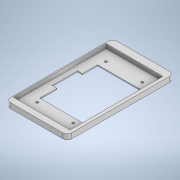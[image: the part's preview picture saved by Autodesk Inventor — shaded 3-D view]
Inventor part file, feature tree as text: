
AUTODESK INVENTOR PART (.ipt)
format: ipt  version: 2021 (Build 250183000, 183)  size: 166,912 bytes
history: native  units: mm
features: extrude x3, sketch x3, projected_geometry x1
ambient origin geometry x8: Origin, YZ Plane, XZ Plane, XY Plane, X Axis, Y Axis, Z Axis, Center Point
bodies: Solid1 (feature_tree)
feature tree (7):
  extrude  "Extrusion1"  Depth=193.2mm
  extrude  "Extrusion2"  Depth=4.2mm
  extrude  "Extrusion3"  Depth=7.5mm
  sketch  "Sketch1"  dims[d0=110.94mm d1=193.2mm]
  sketch  "Sketch2"  dims[d2=4.2mm d3=4.2mm]
  projected_geometry  "Projected Loop1"
  sketch  "Sketch3"  dims[d4=65.3mm d5=65.697mm d6=4.2mm d7=4.2mm d8=126.2mm d9=126.501mm d10=0.0mm d11=22.6mm d12=35.0mm d13=8.0mm d14=2.0mm d15=0.0mm d16=2.0mm d17=14.0mm d18=11.0mm d19=6.0mm d20=7.5mm d21=0.0mm d22=105.0mm d23=79.0mm d24=6.0mm d25=30.0mm d26=40.0mm d27=40.0mm d28=9.0mm d29=7.5mm d30=0.0mm]
